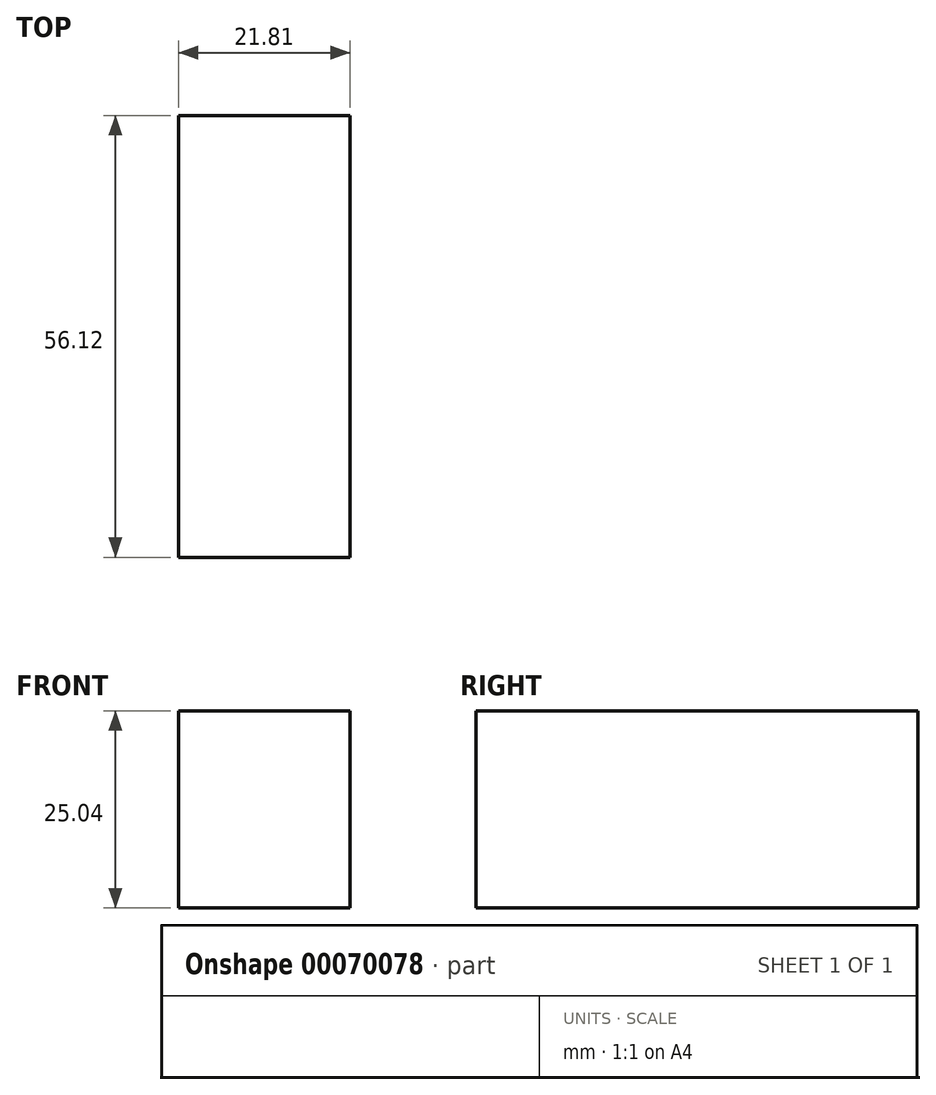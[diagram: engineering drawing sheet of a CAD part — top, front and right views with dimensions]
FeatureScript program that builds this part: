
annotation { "Feature Type Name" : "Feature", "Feature Type Description" : "" }
export const myFeature = defineFeature(function(context is Context, id is Id, definition is map)
    precondition{}
    {
        {
            var Q0;
            Q0=qCreatedBy(makeId("Front.planeOp"),FACE);
            var sketch = newSketch(context, id + "F1", { "sketchPlane" : qUnion([Q0])});
            skLineSegment(sketch, "E0.bottom", {"start": v(-47.08, -52.19) * mm, "end": v(-25.27, -52.19) * mm});
            skLineSegment(sketch, "E0.top", {"start": v(-47.08, -27.15) * mm, "end": v(-25.27, -27.15) * mm});
            skLineSegment(sketch, "E0.left", {"start": v(-47.08, -52.19) * mm, "end": v(-47.08, -27.15) * mm});
            skLineSegment(sketch, "E0.right", {"start": v(-25.27, -52.19) * mm, "end": v(-25.27, -27.15) * mm});
            skSolve(sketch);
        }
        {
            var Q0;
            Q0 = qSketchRegion(id + "F1", true);
            extrude(context, id + "F2", {"entities" : qUnion([Q0]), "depth" : 56.12 * mm});
        }
    });
